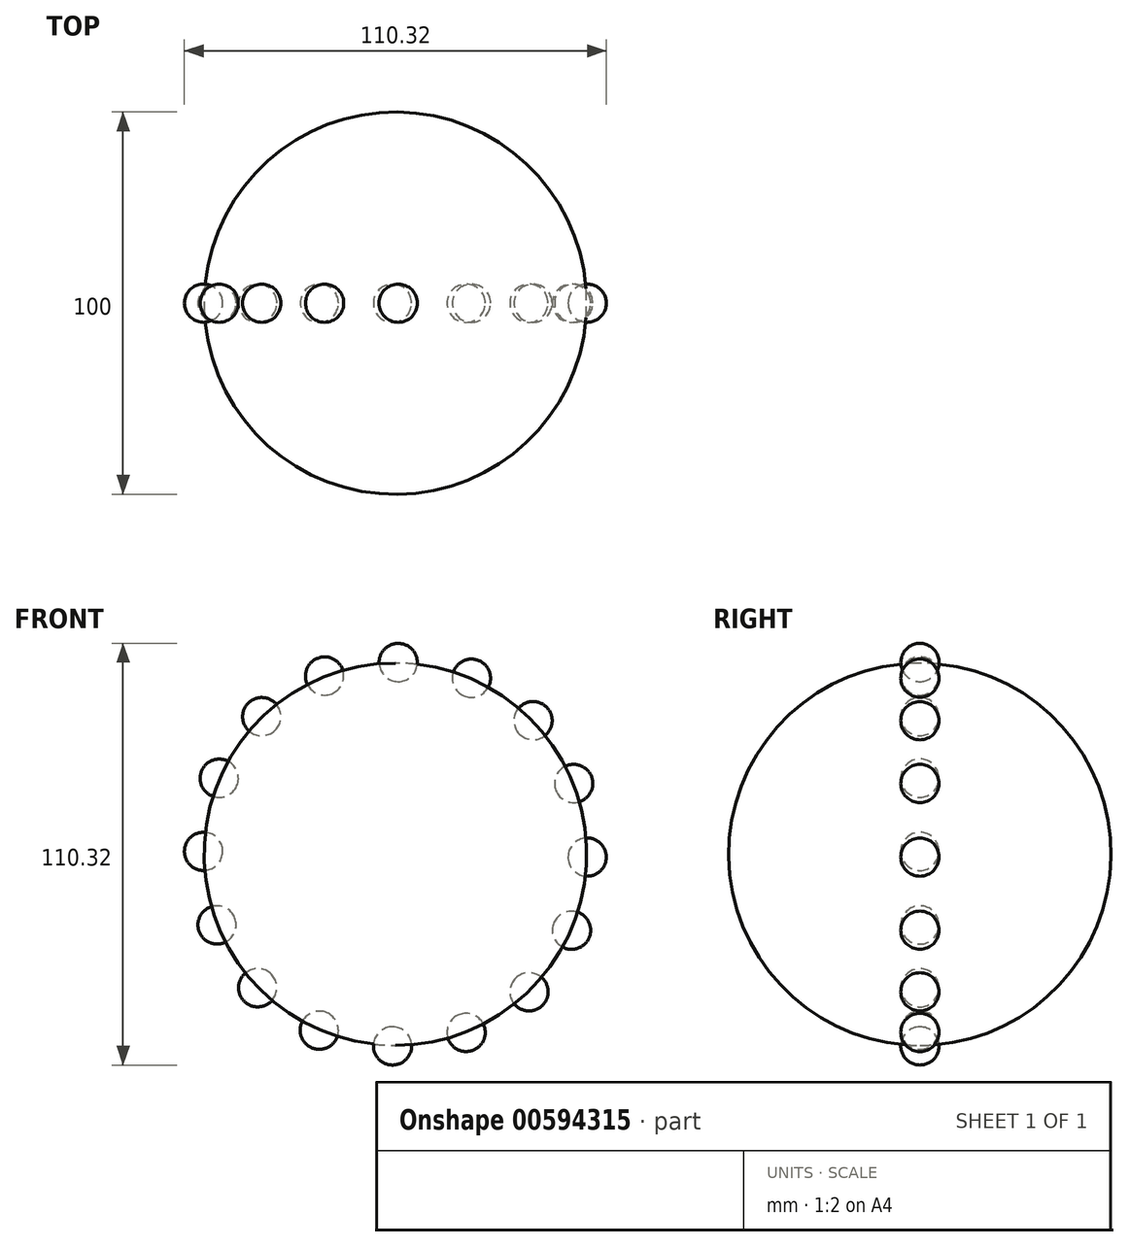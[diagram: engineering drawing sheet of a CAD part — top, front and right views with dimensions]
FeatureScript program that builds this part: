
annotation { "Feature Type Name" : "Feature", "Feature Type Description" : "" }
export const myFeature = defineFeature(function(context is Context, id is Id, definition is map)
    precondition{}
    {
        {
            var Q0;
            Q0=qCreatedBy(makeId("Front.planeOp"),FACE);
            var sketch = newSketch(context, id + "F0", { "sketchPlane" : qUnion([Q0])});
            skCircle(sketch, "E0", {"center": v(0, 0) * mm, "radius": 50 * mm});
            skLineSegment(sketch, "E1", {"start": v(0, 65.41) * mm, "end": v(0, -54.7) * mm});
            skSolve(sketch);
        }
        {
            var Q0;
            {var subQ0=sQuery(id+"F0.wireOp",EDGE,"E1");var subQ1=sQuery(id+"F0.wireOp",EDGE,"E0");var subQ2=makeQuery(id+"F0.imprint","INTERSECT",VERTEX,{"disambiguationData":[OD(0.0)],"derivedFrom":[subQ1,subQ0]});Q0=makeQuery(id+"F0.imprint","IMPRINT",FACE,{"disambiguationData":[TD([[makeQuery(id+"F0.imprint","IMPRINT",EDGE,{"disambiguationData":[TD([[subQ2,-1.0]])],"derivedFrom":subQ1}),1.0]])]});}
            var Q1;
            Q1=sQuery(id+"F0.wireOp",EDGE,"E1");
            revolve(context, id + "F1", {"entities" : qUnion([Q0]), "axis" : qUnion([Q1]), "revolveType" : RevolveType.FULL});
        }
        {
            var Q0;
            Q0=qCreatedBy(makeId("Front.planeOp"),FACE);
            var sketch = newSketch(context, id + "F2", { "sketchPlane" : qUnion([Q0])});
            skLineSegment(sketch, "E2", {"start": v(-50.64, 21.88) * mm, "end": v(-41.47, 17.9) * mm});
            skCircle(sketch, "E3", {"center": v(-46.05, 19.89) * mm, "radius": 5 * mm});
            skPoint(sketch, "E4.center.orphan", {"position": v(-35.1, 35.82) * mm});
            skPoint(sketch, "E5.center.orphan", {"position": v(-19.6, 46.4) * mm});
            skPoint(sketch, "E6.center.orphan", {"position": v(19.6, 46.4) * mm});
            skPoint(sketch, "E7.center.orphan", {"position": v(35.65, 35.82) * mm});
            skPoint(sketch, "E8.center.orphan", {"position": v(50.24, 0) * mm});
            skPoint(sketch, "E9.center.orphan", {"position": v(35.65, -35.48) * mm});
            skPoint(sketch, "E10.center.orphan", {"position": v(19.6, -46.8) * mm});
            skPoint(sketch, "E11.center.orphan", {"position": v(0, -50.26) * mm});
            skPoint(sketch, "E12.center.orphan", {"position": v(-35.65, -35.48) * mm});
            skPoint(sketch, "E13.center.orphan", {"position": v(-50.24, 0) * mm});
            skPoint(sketch, "E14.center.orphan", {"position": v(0, 50.23) * mm});
            skSolve(sketch);
        }
        {
            var Q0;
            Q0=makeQuery(id+"F2.imprint","IMPRINT",FACE,{"disambiguationData":[TD([[makeQuery(id+"F2.imprint","IMPRINT",EDGE,{"derivedFrom":sQuery(id+"F2.wireOp",EDGE,"E4")}),1.0]])]});
            var Q1;
            {var subQ0=sQuery(id+"F2.wireOp",EDGE,"E2");Q1=makeQuery(id+"F2.imprint","IMPRINT",FACE,{"disambiguationData":[TD([[makeQuery(id+"F2.imprint","IMPRINT",EDGE,{"derivedFrom":subQ0}),1.0]])]});}
            var Q2;
            Q2=sQuery(id+"F2.wireOp",EDGE,"E2");
            revolve(context, id + "F3", {"entities" : qUnion([Q0, Q1]), "axis" : qUnion([Q2]), "revolveType" : RevolveType.FULL});
        }
        {
            var Q0;
            Q0=qCreatedBy(makeId("Right.planeOp"),FACE);
            var sketch = newSketch(context, id + "F4", { "sketchPlane" : qUnion([Q0])});
            skLineSegment(sketch, "E15", {"start": v(75.04, 0) * mm, "end": v(-74.86, 0) * mm});
            skSolve(sketch);
        }
        {
            var Q0;
            Q0=makeQuery(id+"F3.opRevolve","SWEPT_BODY",BODY,{"disambiguationData":[OSD([sQuery(id+"F2.wireOp",EDGE,"E2"),sQuery(id+"F2.wireOp",EDGE,"E3")])]});
            var Q1;
            Q1=sQuery(id+"F4.wireOp",EDGE,"E15");
            circularPattern(context, id + "F5", {"entities" : qUnion([Q0]), "axis" : qUnion([Q1]), "angle" : 360 * degree, "instanceCount" : 16, "equalSpace" : true});
        }
    });
